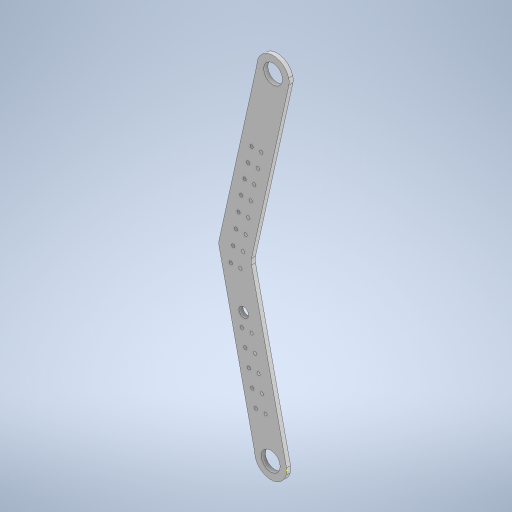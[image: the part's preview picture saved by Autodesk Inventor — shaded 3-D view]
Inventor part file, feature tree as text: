
AUTODESK INVENTOR PART (.ipt)
format: ipt  version: 2023 (Build 270158000, 158)  size: 446,464 bytes
history: native  units: in
note: dims shown in document units (in); Inventor stores cm internally (conversion verified against a paired STEP export)
features: sketch x9, extrude x8, fillet x1, projected_geometry x1
ambient origin geometry x8: Origin, YZ Plane, XZ Plane, XY Plane, X Axis, Y Axis, Z Axis, Center Point
bodies: Body1 (feature_tree)
feature tree (19):
  extrude  "Extrusion3"  Depth=0.7043in
  sketch  "Sketch3"  dims[d0=4.5in d1=0.7043in]
  extrude  "Extrusion14"  Depth=1.0651in
  extrude  "Extrusion15"  Depth=1.0in
  extrude  "Extrusion16"  Depth=0.5in
  extrude  "Extrusion17"  Depth=0.5in
  extrude  "Extrusion18"  Depth=0.5in
  extrude  "Extrusion19"  Depth=1.0in
  extrude  "Extrusion20"  Depth=0.5in
  sketch  "Sketch11"  dims[d25=0.5325in d26=1.0in]
  sketch  "Sketch12"  dims[d27=1.0in d28=0.5in d29=0.5in]
  fillet  "Fillet1"  Radius=0.5in
  sketch  "Sketch13"  dims[d30=0.25in d31=0.0in d42=1.0in d50=1.5in d51=0.25in d59=0.3in d76=0.585in d77=0.585in d78=1.0in d79=0.0in d82=0.1in d83=1.0in d84=0.0in d89=1.0in d90=0.5325in d91=0.5in d92=0.5in d93=0.5in d94=0.5in d95=0.1in d96=0.1in d97=0.1in d98=0.1in d99=0.1in d100=1.0in d101=0.0in d102=0.6in d103=0.1in d104=1.0in d105=0.0in d106=0.125in d107=0.0in d108=2.0in d109=0.3in d110=0.3in d111=0.3in d112=0.3in d113=0.3in d114=0.3in d115=0.3in d116=0.1in d117=0.1in d118=0.1in d119=0.1in d120=0.1in d121=0.1in d122=0.1in d123=0.5in d124=0.5in d125=0.5in d126=0.5in d127=0.5325in d128=0.5in d129=0.5in d130=0.3in d131=0.3in d132=0.3in d133=0.3in d134=0.3in d135=0.3in d136=0.3in d137=0.1in d138=0.1in d139=0.1in d140=0.1in d141=0.1in d142=0.1in d143=0.1in d144=0.1in d145=0.1in d146=0.1in d147=0.1in d148=0.1in d149=0.1in d150=0.1in d151=0.125in d152=0.0in d153=0.125in d154=0.0in d155=0.4in d60=0.0344in d61=0.5in d62=0.0344in d74=0.5in d75=0.0344in d80=0.5in d81=0.0344in]
  sketch  "Sketch6"  dims[d2=4.5in d3=1.0651in]
  sketch  "Sketch7"  dims[d4=1.0in d5=1.0in]
  sketch  "Sketch8"  dims[d6=1.0in d7=0.5in]
  projected_geometry  "Projected Loop1"
  sketch  "Sketch9"  dims[d8=0.5in d9=0.5in]
  sketch  "Sketch10"  dims[d10=0.5in d24=5.5in]
